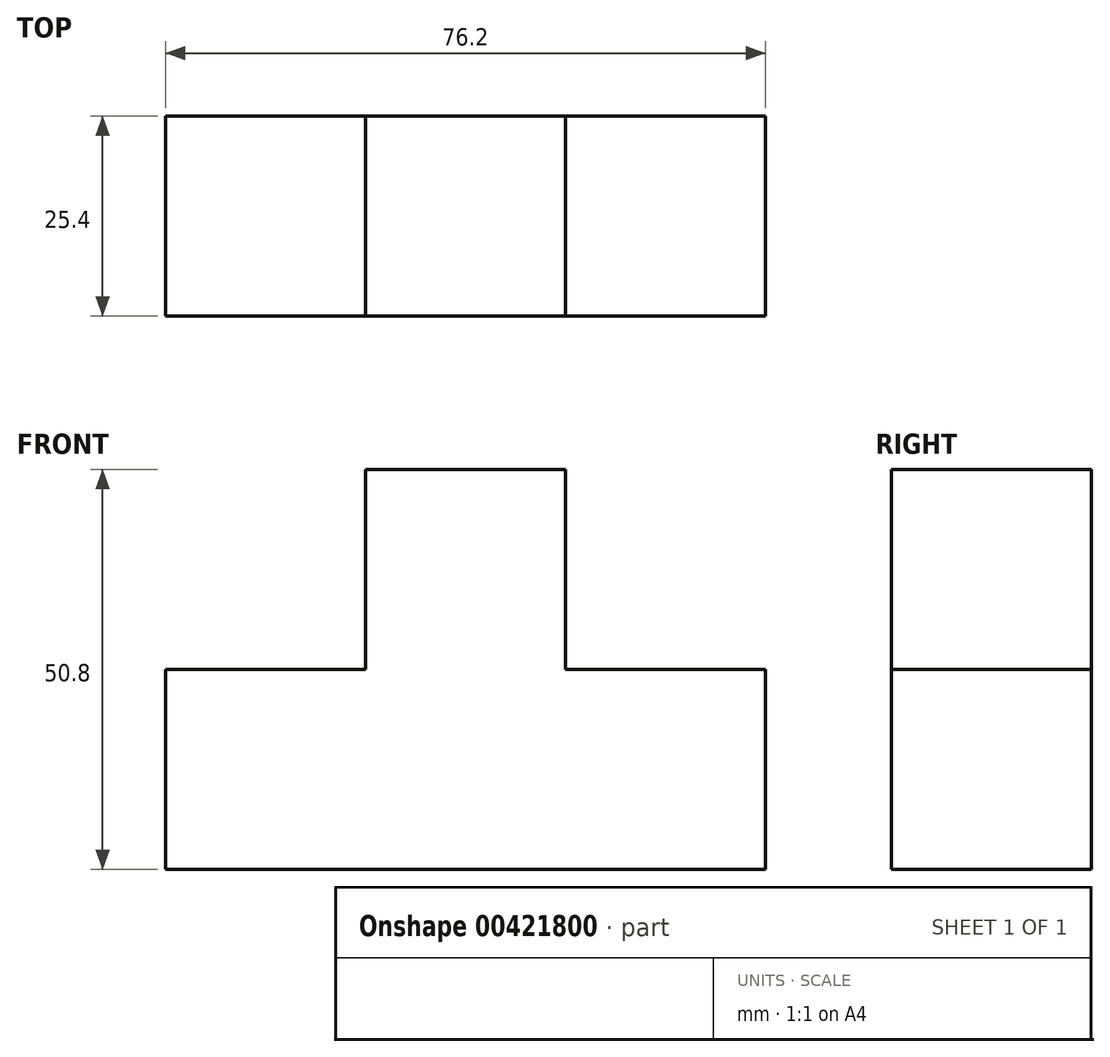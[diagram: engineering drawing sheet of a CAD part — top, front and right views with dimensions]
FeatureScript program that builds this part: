
annotation { "Feature Type Name" : "Feature", "Feature Type Description" : "" }
export const myFeature = defineFeature(function(context is Context, id is Id, definition is map)
    precondition{}
    {
        {
            var Q0;
            Q0=qCreatedBy(makeId("Front.planeOp"),FACE);
            var sketch = newSketch(context, id + "F0", { "sketchPlane" : qUnion([Q0])});
            skLineSegment(sketch, "E0", {"start": v(0, 0) * mm, "end": v(-76.2, 0) * mm});
            skLineSegment(sketch, "E1", {"start": v(-76.2, 0) * mm, "end": v(-76.2, 25.4) * mm});
            skLineSegment(sketch, "E2", {"start": v(-76.2, 25.4) * mm, "end": v(-50.8, 25.4) * mm});
            skLineSegment(sketch, "E3", {"start": v(-50.8, 25.4) * mm, "end": v(-50.8, 50.8) * mm});
            skLineSegment(sketch, "E4", {"start": v(-50.8, 50.8) * mm, "end": v(-25.4, 50.8) * mm});
            skLineSegment(sketch, "E5", {"start": v(-25.4, 50.8) * mm, "end": v(-25.4, 25.4) * mm});
            skLineSegment(sketch, "E6", {"start": v(-25.4, 25.4) * mm, "end": v(0, 25.4) * mm});
            skLineSegment(sketch, "E7", {"start": v(0, 25.4) * mm, "end": v(0, 0) * mm});
            skSolve(sketch);
        }
        {
            var Q0;
            Q0 = qSketchRegion(id + "F0", true);
            extrude(context, id + "F1", {"entities" : qUnion([Q0]), "depth" : 25.4 * mm});
        }
    });
